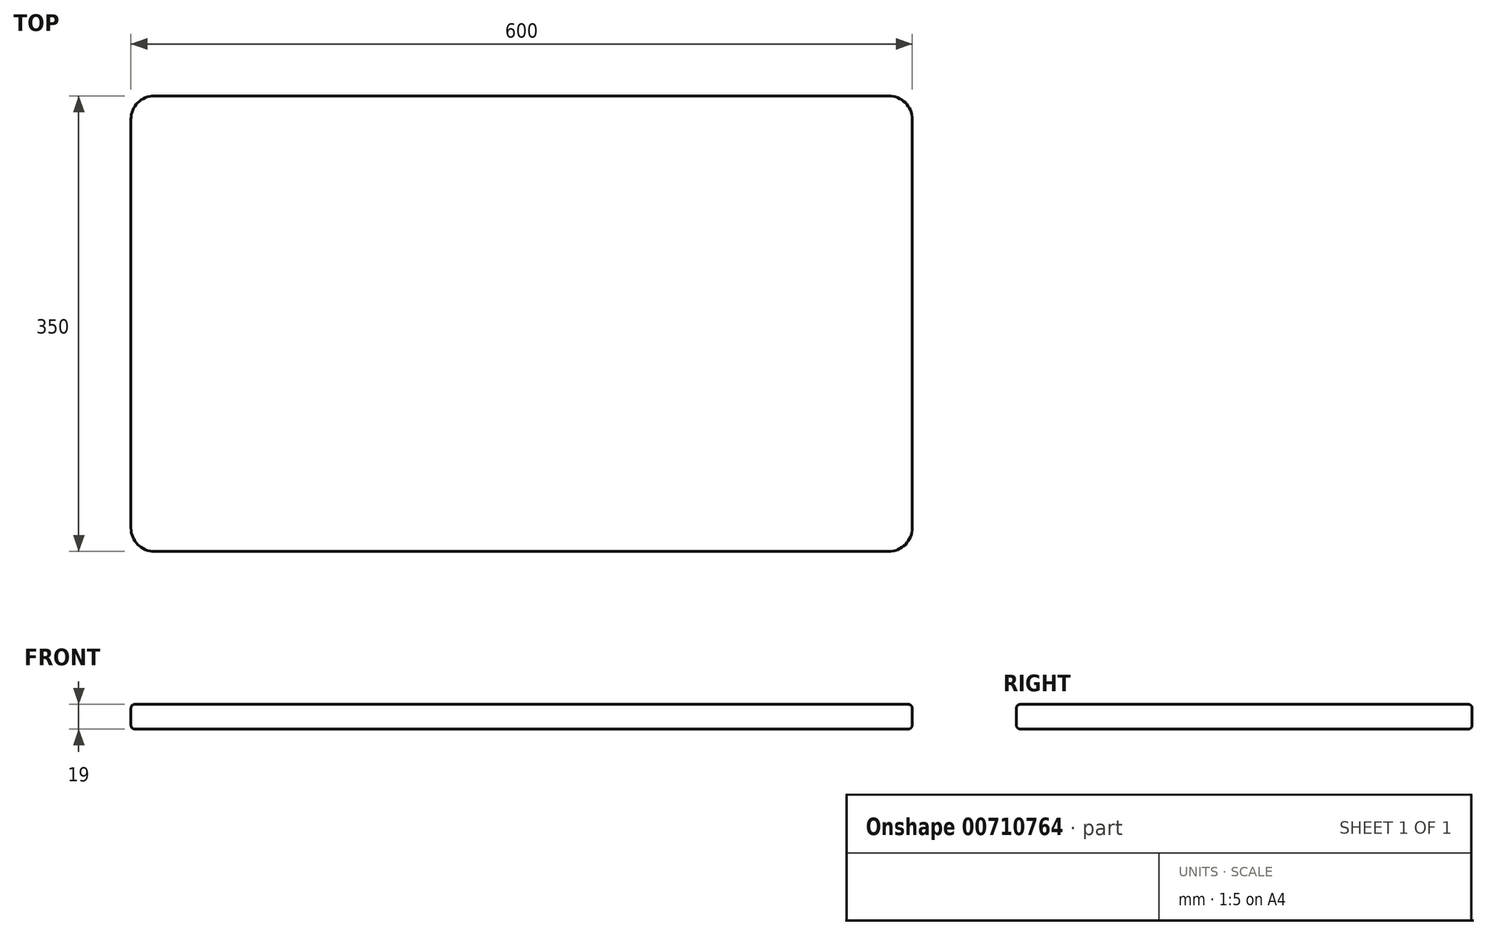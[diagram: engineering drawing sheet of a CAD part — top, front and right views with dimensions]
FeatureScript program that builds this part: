
annotation { "Feature Type Name" : "Feature", "Feature Type Description" : "" }
export const myFeature = defineFeature(function(context is Context, id is Id, definition is map)
    precondition{}
    {
        {
            var Q0;
            Q0=qCreatedBy(makeId("Top.planeOp"),FACE);
            var sketch = newSketch(context, id + "F0", { "sketchPlane" : qUnion([Q0])});
            skLineSegment(sketch, "E0.bottom", {"start": v(-327.98, 216.67) * mm, "end": v(272.02, 216.67) * mm});
            skLineSegment(sketch, "E0.top", {"start": v(-327.98, -133.33) * mm, "end": v(272.02, -133.33) * mm});
            skLineSegment(sketch, "E0.left", {"start": v(-327.98, 216.67) * mm, "end": v(-327.98, -133.33) * mm});
            skLineSegment(sketch, "E0.right", {"start": v(272.02, 216.67) * mm, "end": v(272.02, -133.33) * mm});
            skSolve(sketch);
        }
        {
            var Q0;
            Q0=makeQuery(id+"F0.imprint","IMPRINT",FACE,{"disambiguationData":[TD([[makeQuery(id+"F0.imprint","IMPRINT",EDGE,{"derivedFrom":sQuery(id+"F0.wireOp",EDGE,"E0.bottom")}),-1.0]])]});
            extrude(context, id + "F1", {"entities" : qUnion([Q0]), "depth" : 19 * mm, "offsetDistance" : 25 * mm});
        }
        {
            var Q0;
            Q0=makeQuery(id+"F1.opExtrude","CAP_EDGE",EDGE,{"disambiguationData":[OSD([sQuery(id+"F0.wireOp",EDGE,"E0.top")])],"isStart":false});
            var Q1;
            Q1=makeQuery(id+"F1.opExtrude","CAP_EDGE",EDGE,{"disambiguationData":[OSD([sQuery(id+"F0.wireOp",EDGE,"E0.left")])],"isStart":false});
            var Q2;
            Q2=makeQuery(id+"F1.opExtrude","CAP_EDGE",EDGE,{"disambiguationData":[OSD([sQuery(id+"F0.wireOp",EDGE,"E0.bottom")])],"isStart":false});
            var Q3;
            Q3=makeQuery(id+"F1.opExtrude","CAP_EDGE",EDGE,{"disambiguationData":[OSD([sQuery(id+"F0.wireOp",EDGE,"E0.right")])],"isStart":false});
            var Q4;
            Q4=makeQuery(id+"F1.opExtrude","CAP_EDGE",EDGE,{"disambiguationData":[OSD([sQuery(id+"F0.wireOp",EDGE,"E0.top")])],"isStart":true});
            var Q5;
            Q5=makeQuery(id+"F1.opExtrude","CAP_EDGE",EDGE,{"disambiguationData":[OSD([sQuery(id+"F0.wireOp",EDGE,"E0.left")])],"isStart":true});
            var Q6;
            Q6=makeQuery(id+"F1.opExtrude","CAP_EDGE",EDGE,{"disambiguationData":[OSD([sQuery(id+"F0.wireOp",EDGE,"E0.right")])],"isStart":true});
            var Q7;
            Q7=makeQuery(id+"F1.opExtrude","CAP_EDGE",EDGE,{"disambiguationData":[OSD([sQuery(id+"F0.wireOp",EDGE,"E0.bottom")])],"isStart":true});
            fillet(context, id + "F2", {"entities" : qUnion([Q0, Q1, Q2, Q3, Q4, Q5, Q6, Q7]), "radius" : 3 * mm, "tangentPropagation" : true, "allowEdgeOverflow" : false});
        }
        {
            var Q0;
            Q0=makeQuery(id+"F1.opExtrude","SWEPT_EDGE",EDGE,{"disambiguationData":[OSD([sQuery(id+"F0.wireOp",EDGE,"E0.bottom"),sQuery(id+"F0.wireOp",EDGE,"E0.left")])]});
            var Q1;
            Q1=makeQuery(id+"F1.opExtrude","SWEPT_EDGE",EDGE,{"disambiguationData":[OSD([sQuery(id+"F0.wireOp",EDGE,"E0.bottom"),sQuery(id+"F0.wireOp",EDGE,"E0.right")])]});
            var Q2;
            Q2=makeQuery(id+"F1.opExtrude","SWEPT_EDGE",EDGE,{"disambiguationData":[OSD([sQuery(id+"F0.wireOp",EDGE,"E0.top"),sQuery(id+"F0.wireOp",EDGE,"E0.left")])]});
            var Q3;
            Q3=makeQuery(id+"F1.opExtrude","SWEPT_EDGE",EDGE,{"disambiguationData":[OSD([sQuery(id+"F0.wireOp",EDGE,"E0.top"),sQuery(id+"F0.wireOp",EDGE,"E0.right")])]});
            fillet(context, id + "F3", {"entities" : qUnion([Q0, Q1, Q2, Q3]), "radius" : 18 * mm, "tangentPropagation" : true, "allowEdgeOverflow" : false});
        }
    });
